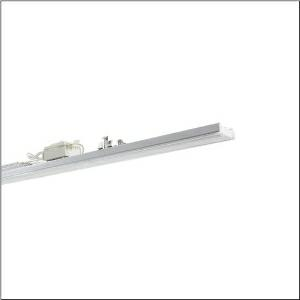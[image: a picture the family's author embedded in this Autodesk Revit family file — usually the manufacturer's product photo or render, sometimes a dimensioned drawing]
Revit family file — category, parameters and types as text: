
# Revit family: licross_r__21_recessed_mo_52te197n48xg_029e
name_source: partatom
category: Lighting Fixtures
units: mm (PartAtom-declared; Revit-internal decimal feet)

## family parameters
Cut with Voids When Loaded = No
Host = Face
Light Source = No
Part Type = Normal
Room Calculation Point = No
Round Connector Dimension = Use Diameter
Shared = No

## types (1)
- Licross® 21 Recessed MO (1 x LED, 8450 lm, 47.9 W, 4000K)
    Apparent Load = 48 VA
    CIE Flux Codes = 55 90 98 100 100
    Color Rendering = 80
    Color Temperature = 4000K
    Default Elevation = 1800 mm
    Description = Licross® 21 Recessed MO, luminaire insert, of sheet steel, galvanised, coil coated, white, length: 1.500mm, width: 66mm, height: 67mm, LED rated luminous flux: 8.450lm, light colour: 840, control gear: ON/OFF, with plug, 3-pole, with phase selection, mains connection: 220..240V, AC, 50/60Hz, rated input power: 48W, internal wiring halogen-free, primary light control with lens, of plastic, primary optical cover: cover, of PMMA, light emission: direct distribution, primary light characteristic: double asymmetric, protection rating (complete): IP54, insulation class (complete): insulation class I (protective earthing), certification: CE, ENEC, VDE, UKCA, protection symbol: D if used in an environment with non-conductive dust loads with corresponding accessories, impact resistance: IK06, permissible ambient temperature for indoor applications: -35..+40°C, corresponds to IFS (International Featured Standards) requirements for safety and quality in the food industry, reducing of maximum allowable ambient temperature of 5°C with ceiling mounting, LABS conformity tested according to VDMA 24364:2018-05, packaging unit: 1 piece
    Height = 58 mm
    Lamp = 1 x LED
    Lamp Light Flux = 8450 lm
    Lamp Power = 47.9 W
    Lamp count = 1
    Length = 1500 mm
    Luminous efficacy = 176 lm/W
    Manufacturer = Siteco
    ModVariant = No
    Model = 52TE197N48XG
    Mounting Place = Ceiling
    Mounting Type = Pendant
    Number of Poles = 1
    OnlyDefault = Yes
    Power Factor = 1
    Product Name = Licross® 21 Recessed MO
    Product group = luminaire insert | ceiling pendant
    ProductGroupID = 902
    Protection Class = Protection class I
    Protection Degree = IP 54
    RLX_Detail_Level = 1
    RLX_Emergency_Light_Flux = 0 lm
    RLX_Emergency_Type = 0
    RLX_Emergency_Type_DB = No
    RlxData = <blob elided: 20945 chars, md5=5aaa4f73>
    Socket = socket
    Standby Power = 0 W
    System Light Flux = 8450 lm
    System Power = 48 W
    Type Comments = Product without accessories
    Type Image = l_1296930.jpg
    URL = http://relux.com
    VarID = ---
    Voltage = 0 V
    Weight = 0.00 kg
    Width = 66 mm

## geometry (parser evidence)
native form markers: Blend x4, Sweep x9
no freeform markers — native parametric forms only
